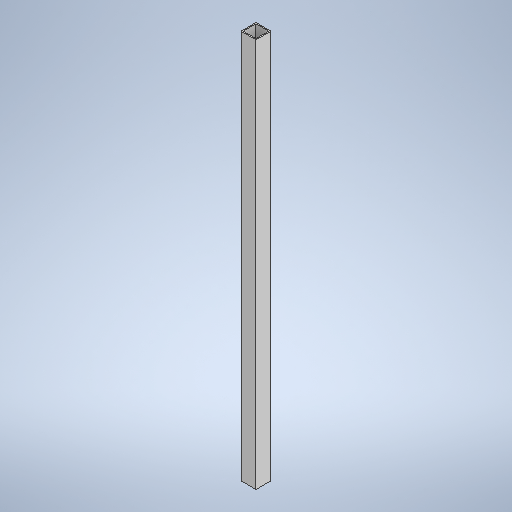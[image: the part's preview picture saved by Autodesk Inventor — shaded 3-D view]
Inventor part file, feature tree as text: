
AUTODESK INVENTOR PART (.ipt)
format: ipt  version: 2025 (Build 290162000, 162)  size: 256,512 bytes
history: native  units: in
note: dims shown in document units (in); Inventor stores cm internally (conversion verified against a paired STEP export)
features: extrude x1, sketch x1
ambient origin geometry x8: Origin, YZ Plane, XZ Plane, XY Plane, X Axis, Y Axis, Z Axis, Center Point
bodies: Solid1 (feature_tree)
feature tree (2):
  extrude  "Extrusion1"  Depth=1.5748in
  sketch  "Sketch1"  dims[d0=1.5748in d1=1.5748in d2=1.3386in d3=1.3386in d4=0.1181in d5=40.9449in d6=0.0in]
